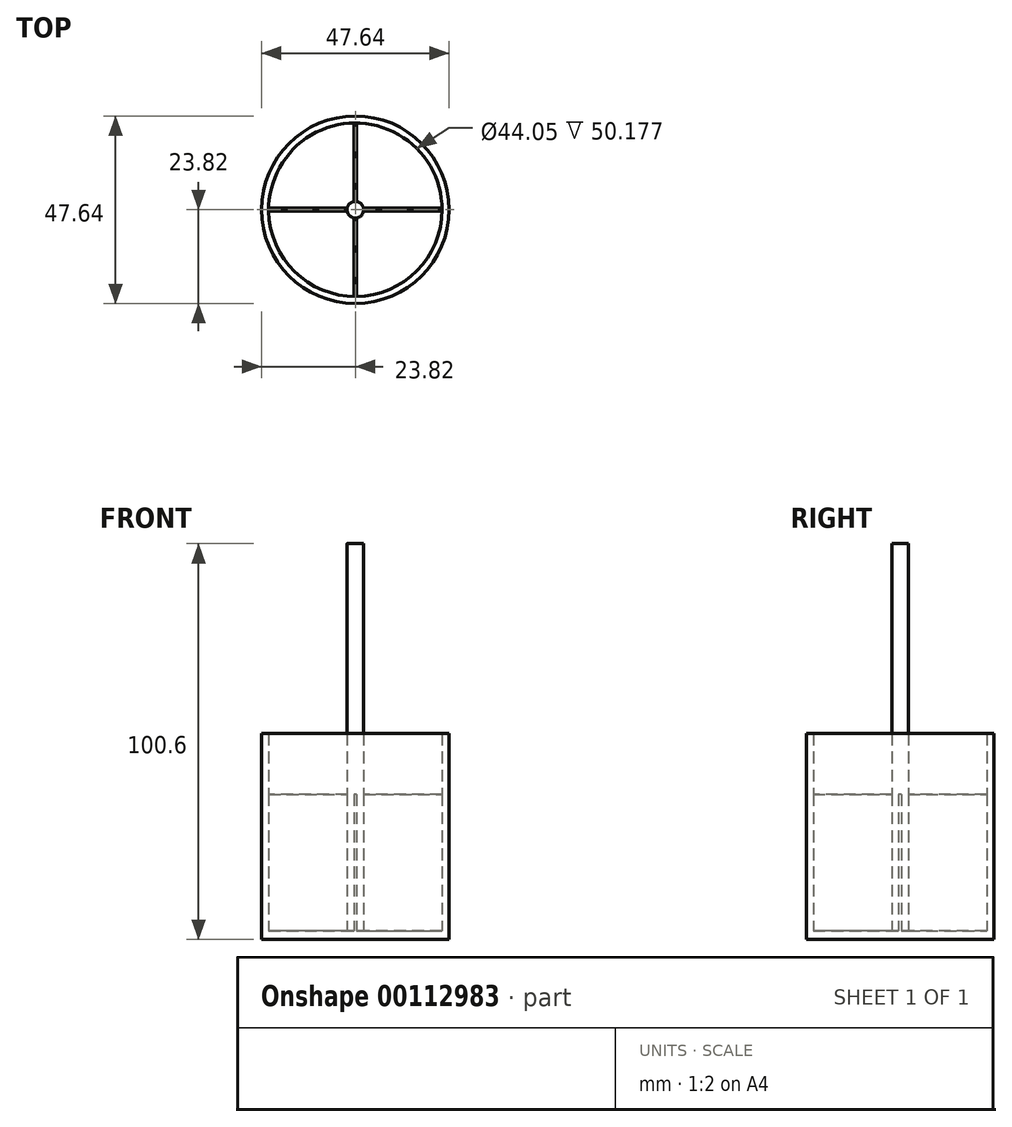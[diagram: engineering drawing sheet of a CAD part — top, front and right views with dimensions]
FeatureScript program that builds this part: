
annotation { "Feature Type Name" : "Feature", "Feature Type Description" : "" }
export const myFeature = defineFeature(function(context is Context, id is Id, definition is map)
    precondition{}
    {
        {
            var Q0;
            Q0=qCreatedBy(makeId("Top.planeOp"),FACE);
            var sketch = newSketch(context, id + "F0", { "sketchPlane" : qUnion([Q0])});
            skCircle(sketch, "E0", {"center": v(0, 0) * mm, "radius": 23.82 * mm});
            skCircle(sketch, "E1", {"center": v(0, 0) * mm, "radius": 22.03 * mm});
            skSolve(sketch);
        }
        {
            var Q0;
            Q0=qCreatedBy(makeId("Top.planeOp"),FACE);
            var sketch = newSketch(context, id + "F1", { "sketchPlane" : qUnion([Q0])});
            skCircle(sketch, "E2", {"center": v(0, 0) * mm, "radius": 2.11 * mm});
            skSolve(sketch);
        }
        {
            var Q0;
            Q0=qCreatedBy(makeId("Top.planeOp"),FACE);
            var sketch = newSketch(context, id + "F2", { "sketchPlane" : qUnion([Q0])});
            skLineSegment(sketch, "E3", {"start": v(23.31, 0.39) * mm, "end": v(-23.27, 0.39) * mm});
            skLineSegment(sketch, "E4", {"start": v(-23.27, 0.39) * mm, "end": v(-23.27, -0.35) * mm});
            skLineSegment(sketch, "E5", {"start": v(-23.27, -0.35) * mm, "end": v(23.31, -0.35) * mm});
            skLineSegment(sketch, "E6", {"start": v(23.31, -0.35) * mm, "end": v(23.31, 0.39) * mm});
            skLineSegment(sketch, "E7", {"start": v(0.36, 23.36) * mm, "end": v(0.36, -23.32) * mm});
            skLineSegment(sketch, "E8", {"start": v(0.36, -23.32) * mm, "end": v(-0.37, -23.32) * mm});
            skLineSegment(sketch, "E9", {"start": v(-0.37, -23.32) * mm, "end": v(-0.37, 23.36) * mm});
            skLineSegment(sketch, "E10", {"start": v(-0.37, 23.36) * mm, "end": v(0.36, 23.36) * mm});
            skSolve(sketch);
        }
        {
            var Q0;
            Q0=makeQuery(id+"F0.imprint","IMPRINT",FACE,{"disambiguationData":[TD([[makeQuery(id+"F0.imprint","IMPRINT",EDGE,{"derivedFrom":sQuery(id+"F0.wireOp",EDGE,"E0")}),1.0]])]});
            extrude(context, id + "F3", {"entities" : qUnion([Q0]), "depth" : 50.18 * mm});
        }
        {
            var Q0;
            Q0=makeQuery(id+"F0.imprint","IMPRINT",FACE,{"disambiguationData":[TD([[makeQuery(id+"F0.imprint","IMPRINT",EDGE,{"derivedFrom":sQuery(id+"F0.wireOp",EDGE,"E1")}),1.0]])]});
            var Q1;
            Q1=makeQuery(id+"F3.opExtrude","CAP_FACE",FACE,{"disambiguationData":[OSD([sQuery(id+"F0.wireOp",EDGE,"E0"),sQuery(id+"F0.wireOp",EDGE,"E1")])],"isStart":false});
            var Q2;
            Q2=makeQuery(id+"F0.imprint","IMPRINT",FACE,{"disambiguationData":[TD([[makeQuery(id+"F0.imprint","IMPRINT",EDGE,{"derivedFrom":sQuery(id+"F0.wireOp",EDGE,"E0")}),1.0]])]});
            var Q3;
            Q3=makeQuery(id+"F3.opExtrude","CAP_FACE",FACE,{"disambiguationData":[OSD([sQuery(id+"F0.wireOp",EDGE,"E0"),sQuery(id+"F0.wireOp",EDGE,"E1")])],"isStart":true});
            extrude(context, id + "F4", {"entities" : qUnion([Q0, Q1, Q2, Q3]), "operationType" : NewBodyOperationType.ADD, "depth" : 2.17 * mm});
        }
        {
            var Q0;
            Q0 = qSketchRegion(id + "F1", true);
            extrude(context, id + "F5", {"entities" : qUnion([Q0]), "operationType" : NewBodyOperationType.ADD, "depth" : 100.6 * mm});
        }
        {
            var Q0;
            Q0 = qSketchRegion(id + "F2", true);
            extrude(context, id + "F6", {"entities" : qUnion([Q0]), "operationType" : NewBodyOperationType.ADD, "depth" : 36.93 * mm});
        }
    });
